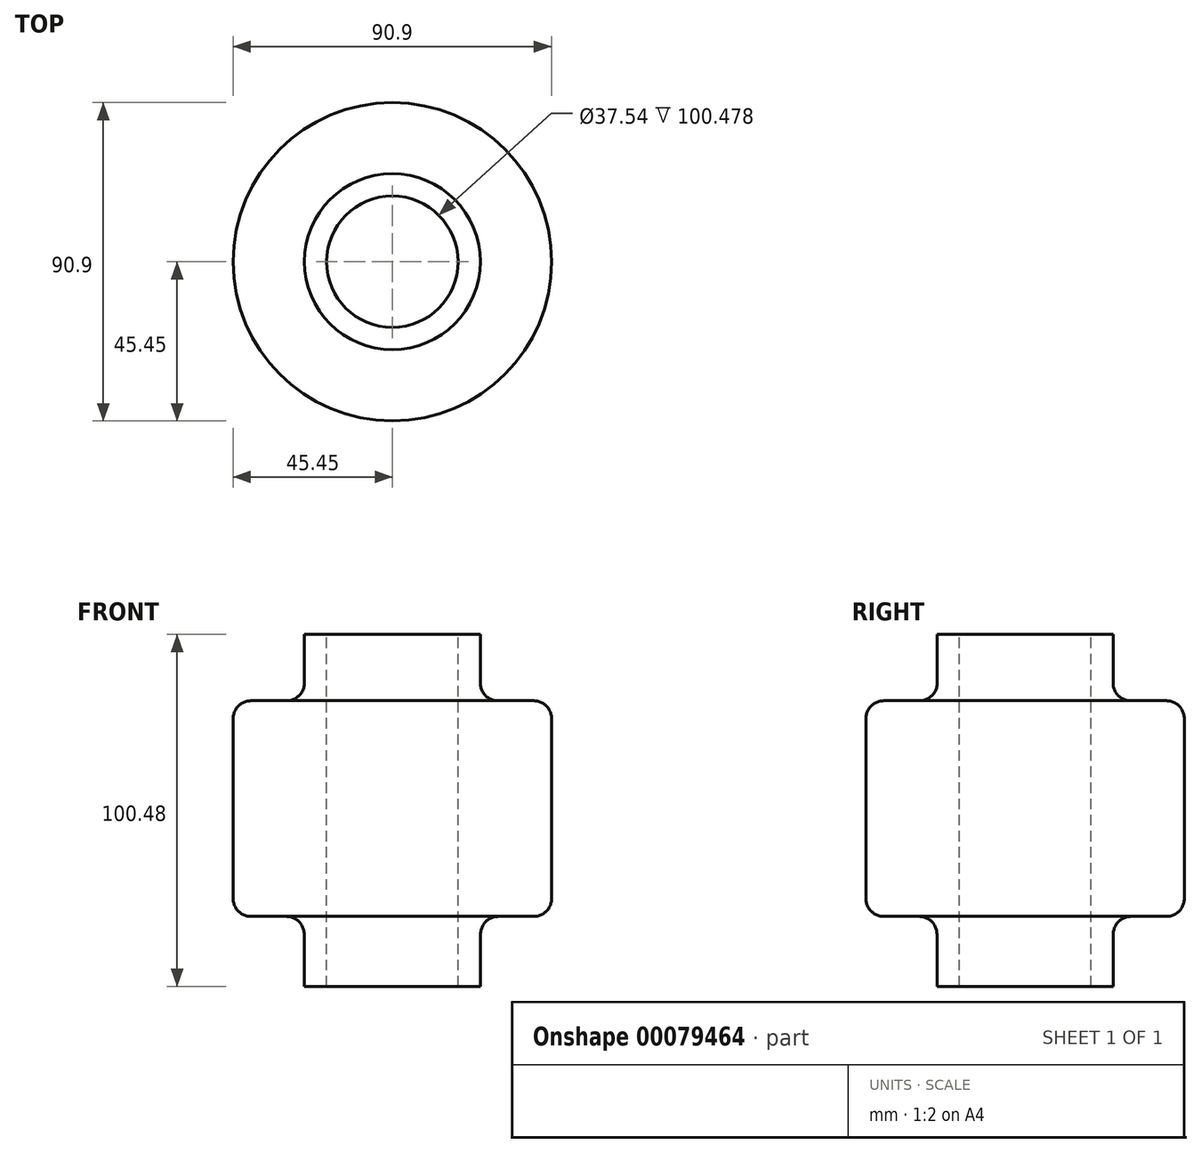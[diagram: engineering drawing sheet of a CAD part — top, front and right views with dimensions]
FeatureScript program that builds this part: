
annotation { "Feature Type Name" : "Feature", "Feature Type Description" : "" }
export const myFeature = defineFeature(function(context is Context, id is Id, definition is map)
    precondition{}
    {
        {
            var Q0;
            Q0=qCreatedBy(makeId("Top.planeOp"),FACE);
            var sketch = newSketch(context, id + "F0", { "sketchPlane" : qUnion([Q0])});
            skCircle(sketch, "E0", {"center": v(0, 0) * mm, "radius": 45.45 * mm});
            skSolve(sketch);
        }
        {
            var Q0;
            Q0 = qSketchRegion(id + "F0", true);
            extrude(context, id + "F1", {"entities" : qUnion([Q0]), "depth" : 61.6 * mm});
        }
        {
            var Q0;
            Q0=makeQuery(id+"F1.opExtrude","CAP_FACE",FACE,{"disambiguationData":[OSD([sQuery(id+"F0.wireOp",EDGE,"E0")])],"isStart":false});
            var sketch = newSketch(context, id + "F2", { "sketchPlane" : qUnion([Q0])});
            skCircle(sketch, "E1", {"center": v(0, 0) * mm, "radius": 25.11 * mm});
            skSolve(sketch);
        }
        {
            var Q0;
            Q0=makeQuery(id+"F2.imprint","IMPRINT",FACE,{"disambiguationData":[TD([[makeQuery(id+"F2.imprint","IMPRINT",EDGE,{"derivedFrom":sQuery(id+"F2.wireOp",EDGE,"E1")}),1.0]])]});
            var Q1;
            Q1=makeQuery(id+"F1.opExtrude","CAP_FACE",FACE,{"disambiguationData":[OSD([sQuery(id+"F0.wireOp",EDGE,"E0")])],"isStart":true});
            extrude(context, id + "F3", {"entities" : qUnion([Q0, Q1]), "operationType" : NewBodyOperationType.ADD, "depth" : 18.93 * mm});
        }
        {
            var Q0;
            Q0=makeQuery(id+"F1.opExtrude","CAP_FACE",FACE,{"disambiguationData":[OSD([sQuery(id+"F0.wireOp",EDGE,"E0")])],"isStart":true});
            var sketch = newSketch(context, id + "F4", { "sketchPlane" : qUnion([Q0])});
            skCircle(sketch, "E2", {"center": v(0, 0) * mm, "radius": 25.18 * mm});
            skSolve(sketch);
        }
        {
            var Q0;
            Q0 = qSketchRegion(id + "F4", true);
            extrude(context, id + "F5", {"entities" : qUnion([Q0]), "operationType" : NewBodyOperationType.ADD, "depth" : 19.96 * mm});
        }
        {
            var Q0;
            Q0=makeQuery(id+"F1.opExtrude","SWEPT_FACE",FACE,{"disambiguationData":[OSD([sQuery(id+"F0.wireOp",EDGE,"E0")])]});
            var Q1;
            Q1=makeQuery(id+"F1.opExtrude","CAP_FACE",FACE,{"disambiguationData":[OSD([sQuery(id+"F0.wireOp",EDGE,"E0")])],"isStart":false});
            var Q2;
            Q2=makeQuery(id+"F1.opExtrude","CAP_FACE",FACE,{"disambiguationData":[OSD([sQuery(id+"F0.wireOp",EDGE,"E0")])],"isStart":true});
            fillet(context, id + "F6", {"entities" : qUnion([Q0, Q1, Q2]), "radius" : 5.08 * mm, "tangentPropagation" : true, "allowEdgeOverflow" : false});
        }
        {
            var Q0;
            Q0=makeQuery(id+"F3.opExtrude","CAP_FACE",FACE,{"disambiguationData":[OSD([sQuery(id+"F2.wireOp",EDGE,"E1")])],"isStart":false});
            var sketch = newSketch(context, id + "F7", { "sketchPlane" : qUnion([Q0])});
            skCircle(sketch, "E3", {"center": v(0, 0) * mm, "radius": 18.77 * mm});
            skSolve(sketch);
        }
        {
            var Q0;
            Q0 = qSketchRegion(id + "F7", true);
            extrude(context, id + "F8", {"entities" : qUnion([Q0]), "operationType" : NewBodyOperationType.REMOVE, "oppositeDirection" : true, "depth" : 284.9 * mm});
        }
    });
